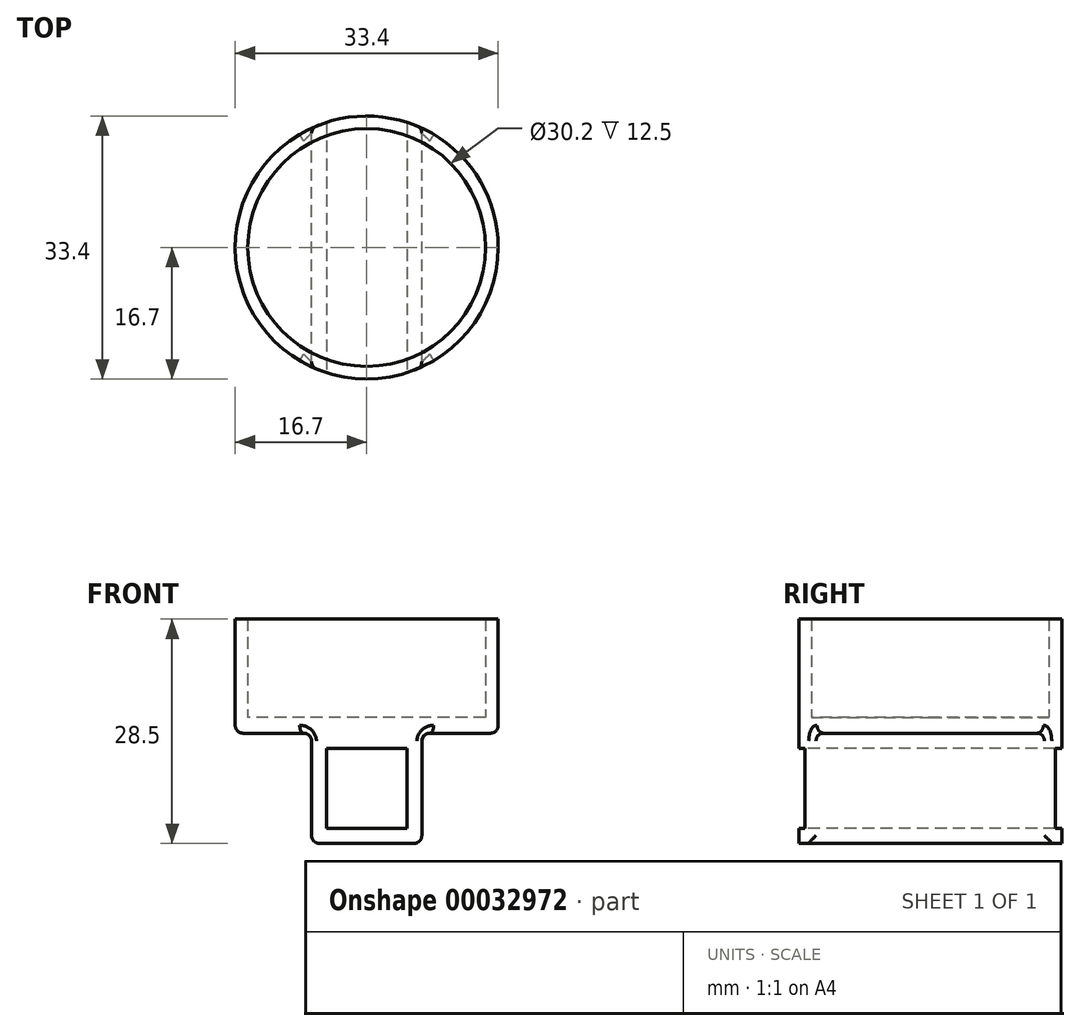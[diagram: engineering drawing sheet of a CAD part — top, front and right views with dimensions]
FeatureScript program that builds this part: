
annotation { "Feature Type Name" : "Feature", "Feature Type Description" : "" }
export const myFeature = defineFeature(function(context is Context, id is Id, definition is map)
    precondition{}
    {
        {
            var Q0;
            Q0=qCreatedBy(makeId("Top.planeOp"),FACE);
            var sketch = newSketch(context, id + "F0", { "sketchPlane" : qUnion([Q0])});
            skCircle(sketch, "E0", {"center": v(0, 0) * mm, "radius": 15.1 * mm});
            skCircle(sketch, "E1.0", {"center": v(0, 0) * mm, "radius": 16.7 * mm});
            skSolve(sketch);
        }
        {
            var Q0;
            Q0=qSketchRegion(id+"F0",true);
            extrude(context, id + "F1", {"entities" : qUnion([Q0]), "depth" : 12.5 * mm});
        }
        {
            var Q0;
            Q0=qCreatedBy(makeId("Top.planeOp"),FACE);
            var sketch = newSketch(context, id + "F2", { "sketchPlane" : qUnion([Q0])});
            skCircle(sketch, "E2", {"center": v(0, 0) * mm, "radius": 16.7 * mm});
            skSolve(sketch);
        }
        {
            var Q0;
            Q0=qSketchRegion(id+"F2",true);
            extrude(context, id + "F3", {"entities" : qUnion([Q0]), "operationType" : NewBodyOperationType.ADD, "oppositeDirection" : true, "depth" : 2 * mm});
        }
        {
            var Q0;
            Q0=makeQuery(id+"F3.opExtrude","CAP_FACE",FACE,{"disambiguationData":[OSD([sQuery(id+"F2.wireOp",EDGE,"E2")])],"isStart":false});
            var sketch = newSketch(context, id + "F4", { "sketchPlane" : qUnion([Q0])});
            skLineSegment(sketch, "E3.rect.left", {"start": v(7, 15.16) * mm, "end": v(7, -15.16) * mm});
            skLineSegment(sketch, "E3.rect.right", {"start": v(-7, 15.16) * mm, "end": v(-7, -15.16) * mm});
            skPoint(sketch, "E3.rect.middle", {"position": v(0, 0) * mm});
            skArc(sketch, "E4", {"start": v(7, 15.16) * mm, "mid": v(0, 16.7) * mm, "end": v(-7, 15.16) * mm});
            skArc(sketch, "E5.MirrorCS", {"start": v(7, -15.16) * mm, "mid": v(0, -16.7) * mm, "end": v(-7, -15.16) * mm});
            skSolve(sketch);
        }
        {
            var Q0;
            Q0=qSketchRegion(id+"F4",true);
            extrude(context, id + "F5", {"entities" : qUnion([Q0]), "operationType" : NewBodyOperationType.ADD, "depth" : 14 * mm});
        }
        {
            var Q0;
            Q0=qCreatedBy(makeId("Front.planeOp"),FACE);
            var sketch = newSketch(context, id + "F6", { "sketchPlane" : qUnion([Q0])});
            skLineSegment(sketch, "E6.0", {"start": v(-5.1, -14.1) * mm, "end": v(-5.1, -3.9) * mm});
            skLineSegment(sketch, "E6.1", {"start": v(-5.1, -14.1) * mm, "end": v(5.1, -14.1) * mm});
            skLineSegment(sketch, "E6.2", {"start": v(5.1, -14.1) * mm, "end": v(5.1, -3.9) * mm});
            skLineSegment(sketch, "E7", {"start": v(-5.1, -3.9) * mm, "end": v(5.1, -3.9) * mm});
            skSolve(sketch);
        }
        {
            var Q0;
            Q0=qSketchRegion(id+"F6",true);
            extrude(context, id + "F7", {"entities" : qUnion([Q0]), "operationType" : NewBodyOperationType.REMOVE, "oppositeDirection" : true, "depth" : 50 * mm, "symmetric" : true});
        }
        {
            var Q0;
            {var subQ0=sQuery(id+"F2.wireOp",EDGE,"E2");Q0=makeQuery(id+"F5.boolean.opBoolean","SPLIT",EDGE,{"disambiguationData":[TD([makeQuery(id+"F5.opExtrude","SWEPT_FACE",FACE,{"disambiguationData":[OSD([sQuery(id+"F4.wireOp",EDGE,"E3.rect.left")])]})])],"derivedFrom":makeQuery(id+"F3.opExtrude","CAP_EDGE",EDGE,{"disambiguationData":[OSD([subQ0])],"isStart":false})});}
            var Q1;
            {var subQ0=sQuery(id+"F2.wireOp",EDGE,"E2");Q1=makeQuery(id+"F5.boolean.opBoolean","SPLIT",EDGE,{"disambiguationData":[TD([makeQuery(id+"F5.opExtrude","SWEPT_FACE",FACE,{"disambiguationData":[OSD([sQuery(id+"F4.wireOp",EDGE,"E3.rect.right")])]})])],"derivedFrom":makeQuery(id+"F3.opExtrude","CAP_EDGE",EDGE,{"disambiguationData":[OSD([subQ0])],"isStart":false})});}
            var Q2;
            Q2=makeQuery(id+"F5.opExtrude","SWEPT_FACE",FACE,{"disambiguationData":[OSD([sQuery(id+"F4.wireOp",EDGE,"E3.rect.left")])]});
            var Q3;
            Q3=makeQuery(id+"F5.opExtrude","SWEPT_FACE",FACE,{"disambiguationData":[OSD([sQuery(id+"F4.wireOp",EDGE,"E3.rect.right")])]});
            fillet(context, id + "F8", {"entities" : qUnion([Q0, Q1, Q2, Q3]), "radius" : 1 * mm, "tangentPropagation" : true, "allowEdgeOverflow" : false});
        }
    });
